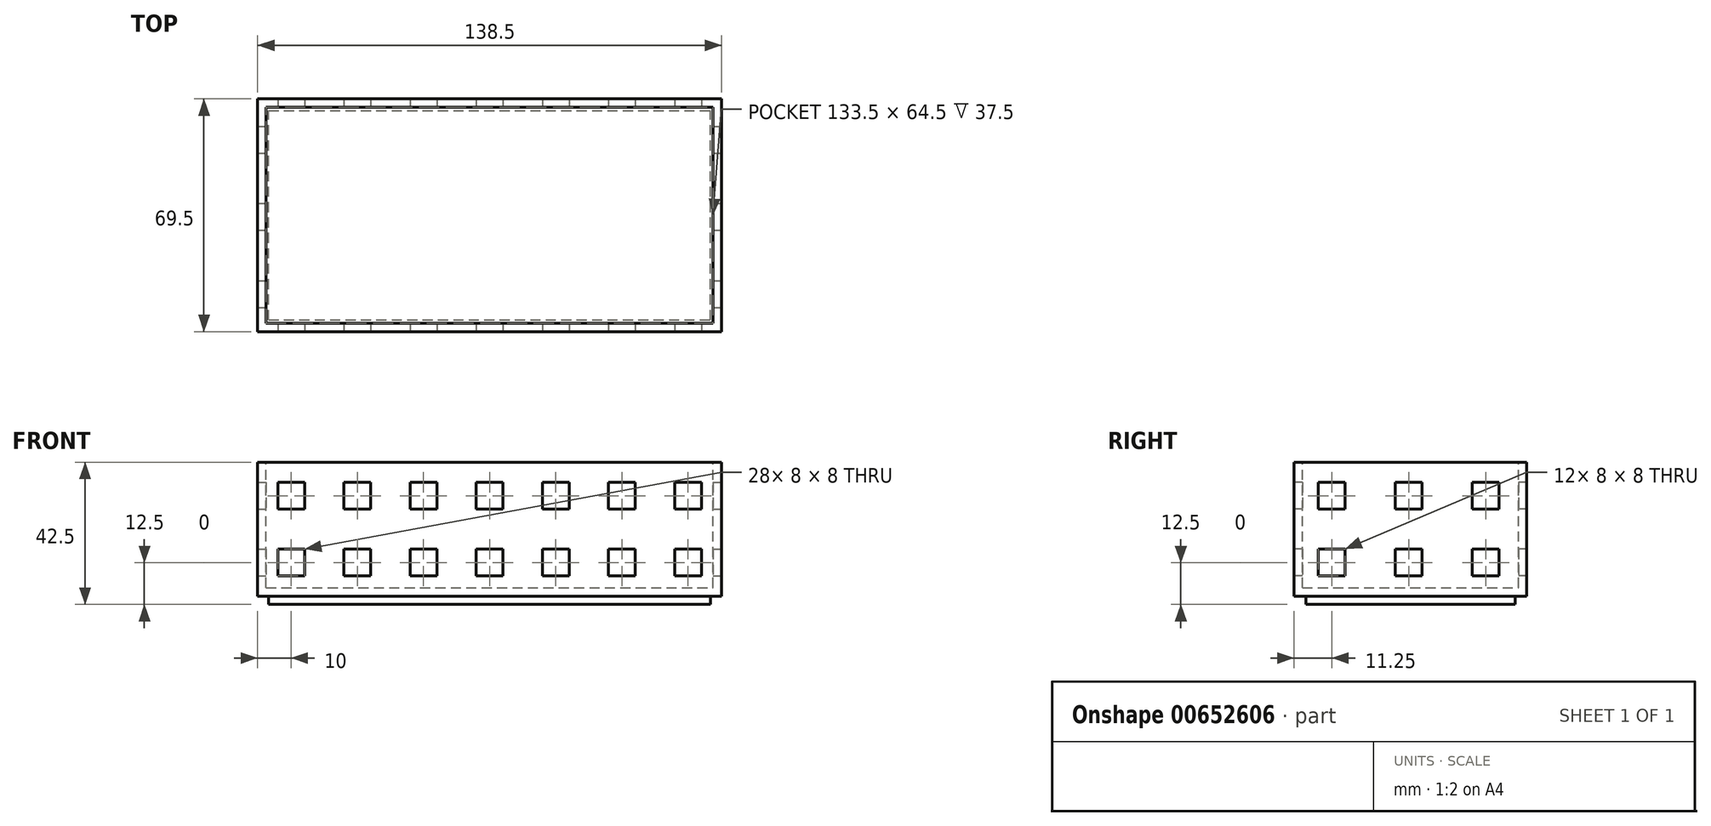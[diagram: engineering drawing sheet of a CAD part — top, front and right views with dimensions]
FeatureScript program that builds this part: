
annotation { "Feature Type Name" : "Feature", "Feature Type Description" : "" }
export const myFeature = defineFeature(function(context is Context, id is Id, definition is map)
    precondition{}
    {
        {
            var Q0;
            Q0=qCreatedBy(makeId("Top.planeOp"),FACE);
            var sketch = newSketch(context, id + "F0", { "sketchPlane" : qUnion([Q0])});
            skLineSegment(sketch, "E0.bottom", {"start": v(0, 0) * mm, "end": v(138.5, 0) * mm});
            skLineSegment(sketch, "E0.top", {"start": v(0, 69.5) * mm, "end": v(138.5, 69.5) * mm});
            skLineSegment(sketch, "E0.left", {"start": v(0, 0) * mm, "end": v(0, 69.5) * mm});
            skLineSegment(sketch, "E0.right", {"start": v(138.5, 0) * mm, "end": v(138.5, 69.5) * mm});
            skSolve(sketch);
        }
        {
            var Q0;
            Q0=makeQuery(id+"F0.imprint","IMPRINT",FACE,{"disambiguationData":[TD([[makeQuery(id+"F0.imprint","IMPRINT",EDGE,{"derivedFrom":sQuery(id+"F0.wireOp",EDGE,"E0.bottom")}),1.0]])]});
            extrude(context, id + "F1", {"entities" : qUnion([Q0]), "depth" : 40 * mm, "offsetDistance" : 25 * mm});
        }
        {
            var Q0;
            Q0=makeQuery(id+"F1.opExtrude","CAP_FACE",FACE,{"disambiguationData":[OSD([sQuery(id+"F0.wireOp",EDGE,"E0.bottom"),sQuery(id+"F0.wireOp",EDGE,"E0.top"),sQuery(id+"F0.wireOp",EDGE,"E0.left"),sQuery(id+"F0.wireOp",EDGE,"E0.right")])],"isStart":false});
            var sketch = newSketch(context, id + "F2", { "sketchPlane" : qUnion([Q0])});
            skLineSegment(sketch, "E1.bottom", {"start": v(2.5, 2.5) * mm, "end": v(136, 2.5) * mm});
            skLineSegment(sketch, "E1.top", {"start": v(2.5, 67) * mm, "end": v(136, 67) * mm});
            skLineSegment(sketch, "E1.left", {"start": v(2.5, 2.5) * mm, "end": v(2.5, 67) * mm});
            skLineSegment(sketch, "E1.right", {"start": v(136, 2.5) * mm, "end": v(136, 67) * mm});
            skSolve(sketch);
        }
        {
            var Q0;
            Q0=makeQuery(id+"F2.imprint","IMPRINT",FACE,{"disambiguationData":[TD([[makeQuery(id+"F2.imprint","IMPRINT",EDGE,{"derivedFrom":sQuery(id+"F2.wireOp",EDGE,"E1.bottom")}),1.0]])]});
            extrude(context, id + "F3", {"entities" : qUnion([Q0]), "operationType" : NewBodyOperationType.REMOVE, "oppositeDirection" : true, "depth" : 37.5 * mm, "offsetDistance" : 25 * mm});
        }
        {
            var Q0;
            Q0=makeQuery(id+"F1.opExtrude","CAP_FACE",FACE,{"disambiguationData":[OSD([sQuery(id+"F0.wireOp",EDGE,"E0.bottom"),sQuery(id+"F0.wireOp",EDGE,"E0.top"),sQuery(id+"F0.wireOp",EDGE,"E0.left"),sQuery(id+"F0.wireOp",EDGE,"E0.right")])],"isStart":true});
            var sketch = newSketch(context, id + "F4", { "sketchPlane" : qUnion([Q0])});
            skLineSegment(sketch, "E2.bottom", {"start": v(3.25, -3.5) * mm, "end": v(135.25, -3.5) * mm});
            skLineSegment(sketch, "E2.top", {"start": v(3.25, -66) * mm, "end": v(135.25, -66) * mm});
            skLineSegment(sketch, "E2.left", {"start": v(3.25, -3.5) * mm, "end": v(3.25, -66) * mm});
            skLineSegment(sketch, "E2.right", {"start": v(135.25, -3.5) * mm, "end": v(135.25, -66) * mm});
            skSolve(sketch);
        }
        {
            var Q0;
            Q0=makeQuery(id+"F4.imprint","IMPRINT",FACE,{"disambiguationData":[TD([[makeQuery(id+"F4.imprint","IMPRINT",EDGE,{"derivedFrom":sQuery(id+"F4.wireOp",EDGE,"E2.bottom")}),-1.0]])]});
            extrude(context, id + "F5", {"entities" : qUnion([Q0]), "operationType" : NewBodyOperationType.ADD, "depth" : 2.5 * mm, "offsetDistance" : 25 * mm});
        }
        {
            var Q0;
            Q0=makeQuery(id+"F1.opExtrude","SWEPT_FACE",FACE,{"disambiguationData":[OSD([sQuery(id+"F0.wireOp",EDGE,"E0.right")])]});
            var sketch = newSketch(context, id + "F6", { "sketchPlane" : qUnion([Q0])});
            skLineSegment(sketch, "E3.bottom", {"start": v(7.25, 34) * mm, "end": v(15.25, 34) * mm});
            skLineSegment(sketch, "E3.top", {"start": v(7.25, 26) * mm, "end": v(15.25, 26) * mm});
            skLineSegment(sketch, "E3.left", {"start": v(7.25, 34) * mm, "end": v(7.25, 26) * mm});
            skLineSegment(sketch, "E3.right", {"start": v(15.25, 34) * mm, "end": v(15.25, 26) * mm});
            skLineSegment(sketch, "E4.bottom", {"start": v(30.25, 34) * mm, "end": v(38.25, 34) * mm});
            skLineSegment(sketch, "E4.top", {"start": v(30.25, 26) * mm, "end": v(38.25, 26) * mm});
            skLineSegment(sketch, "E4.left", {"start": v(30.25, 34) * mm, "end": v(30.25, 26) * mm});
            skLineSegment(sketch, "E4.right", {"start": v(38.25, 34) * mm, "end": v(38.25, 26) * mm});
            skLineSegment(sketch, "E5.bottom", {"start": v(53.25, 34) * mm, "end": v(61.25, 34) * mm});
            skLineSegment(sketch, "E5.top", {"start": v(53.25, 26) * mm, "end": v(61.25, 26) * mm});
            skLineSegment(sketch, "E5.left", {"start": v(53.25, 34) * mm, "end": v(53.25, 26) * mm});
            skLineSegment(sketch, "E5.right", {"start": v(61.25, 34) * mm, "end": v(61.25, 26) * mm});
            skLineSegment(sketch, "E6.bottom", {"start": v(7.25, 14) * mm, "end": v(15.25, 14) * mm});
            skLineSegment(sketch, "E6.top", {"start": v(7.25, 6) * mm, "end": v(15.25, 6) * mm});
            skLineSegment(sketch, "E6.left", {"start": v(7.25, 14) * mm, "end": v(7.25, 6) * mm});
            skLineSegment(sketch, "E6.right", {"start": v(15.25, 14) * mm, "end": v(15.25, 6) * mm});
            skLineSegment(sketch, "E7.bottom", {"start": v(30.25, 14) * mm, "end": v(38.25, 14) * mm});
            skLineSegment(sketch, "E7.top", {"start": v(30.25, 6) * mm, "end": v(38.25, 6) * mm});
            skLineSegment(sketch, "E7.left", {"start": v(30.25, 14) * mm, "end": v(30.25, 6) * mm});
            skLineSegment(sketch, "E7.right", {"start": v(38.25, 14) * mm, "end": v(38.25, 6) * mm});
            skLineSegment(sketch, "E8.bottom", {"start": v(53.25, 14) * mm, "end": v(61.25, 14) * mm});
            skLineSegment(sketch, "E8.top", {"start": v(53.25, 6) * mm, "end": v(61.25, 6) * mm});
            skLineSegment(sketch, "E8.left", {"start": v(53.25, 14) * mm, "end": v(53.25, 6) * mm});
            skLineSegment(sketch, "E8.right", {"start": v(61.25, 14) * mm, "end": v(61.25, 6) * mm});
            skSolve(sketch);
        }
        {
            var Q0;
            Q0=makeQuery(id+"F6.imprint","IMPRINT",FACE,{"disambiguationData":[TD([[makeQuery(id+"F6.imprint","IMPRINT",EDGE,{"derivedFrom":sQuery(id+"F6.wireOp",EDGE,"E3.bottom")}),-1.0]])]});
            var Q1;
            Q1=makeQuery(id+"F6.imprint","IMPRINT",FACE,{"disambiguationData":[TD([[makeQuery(id+"F6.imprint","IMPRINT",EDGE,{"derivedFrom":sQuery(id+"F6.wireOp",EDGE,"E6.bottom")}),-1.0]])]});
            var Q2;
            Q2=makeQuery(id+"F6.imprint","IMPRINT",FACE,{"disambiguationData":[TD([[makeQuery(id+"F6.imprint","IMPRINT",EDGE,{"derivedFrom":sQuery(id+"F6.wireOp",EDGE,"E8.bottom")}),-1.0]])]});
            var Q3;
            Q3=makeQuery(id+"F6.imprint","IMPRINT",FACE,{"disambiguationData":[TD([[makeQuery(id+"F6.imprint","IMPRINT",EDGE,{"derivedFrom":sQuery(id+"F6.wireOp",EDGE,"E5.bottom")}),-1.0]])]});
            var Q4;
            Q4=makeQuery(id+"F6.imprint","IMPRINT",FACE,{"disambiguationData":[TD([[makeQuery(id+"F6.imprint","IMPRINT",EDGE,{"derivedFrom":sQuery(id+"F6.wireOp",EDGE,"E4.bottom")}),-1.0]])]});
            var Q5;
            Q5=makeQuery(id+"F6.imprint","IMPRINT",FACE,{"disambiguationData":[TD([[makeQuery(id+"F6.imprint","IMPRINT",EDGE,{"derivedFrom":sQuery(id+"F6.wireOp",EDGE,"E7.bottom")}),-1.0]])]});
            extrude(context, id + "F7", {"entities" : qUnion([Q0, Q1, Q2, Q3, Q4, Q5]), "operationType" : NewBodyOperationType.REMOVE, "oppositeDirection" : true, "depth" : 138.5 * mm, "offsetDistance" : 25 * mm});
        }
        {
            var Q0;
            Q0=makeQuery(id+"F1.opExtrude","SWEPT_FACE",FACE,{"disambiguationData":[OSD([sQuery(id+"F0.wireOp",EDGE,"E0.bottom")])]});
            var sketch = newSketch(context, id + "F8", { "sketchPlane" : qUnion([Q0])});
            skLineSegment(sketch, "E9.bottom", {"start": v(6, 34) * mm, "end": v(14, 34) * mm});
            skLineSegment(sketch, "E9.top", {"start": v(6, 26) * mm, "end": v(14, 26) * mm});
            skLineSegment(sketch, "E9.left", {"start": v(6, 34) * mm, "end": v(6, 26) * mm});
            skLineSegment(sketch, "E9.right", {"start": v(14, 34) * mm, "end": v(14, 26) * mm});
            skLineSegment(sketch, "E10.bottom", {"start": v(25.75, 34) * mm, "end": v(33.75, 34) * mm});
            skLineSegment(sketch, "E10.top", {"start": v(25.75, 26) * mm, "end": v(33.75, 26) * mm});
            skLineSegment(sketch, "E10.left", {"start": v(25.75, 34) * mm, "end": v(25.75, 26) * mm});
            skLineSegment(sketch, "E10.right", {"start": v(33.75, 34) * mm, "end": v(33.75, 26) * mm});
            skLineSegment(sketch, "E11.bottom", {"start": v(45.5, 34) * mm, "end": v(53.5, 34) * mm});
            skLineSegment(sketch, "E11.top", {"start": v(45.5, 26) * mm, "end": v(53.5, 26) * mm});
            skLineSegment(sketch, "E11.left", {"start": v(45.5, 34) * mm, "end": v(45.5, 26) * mm});
            skLineSegment(sketch, "E11.right", {"start": v(53.5, 34) * mm, "end": v(53.5, 26) * mm});
            skLineSegment(sketch, "E12.bottom", {"start": v(65.25, 34) * mm, "end": v(73.25, 34) * mm});
            skLineSegment(sketch, "E12.top", {"start": v(65.25, 26) * mm, "end": v(73.25, 26) * mm});
            skLineSegment(sketch, "E12.left", {"start": v(65.25, 34) * mm, "end": v(65.25, 26) * mm});
            skLineSegment(sketch, "E12.right", {"start": v(73.25, 34) * mm, "end": v(73.25, 26) * mm});
            skLineSegment(sketch, "E13.bottom", {"start": v(85, 34) * mm, "end": v(93, 34) * mm});
            skLineSegment(sketch, "E13.top", {"start": v(85, 26) * mm, "end": v(93, 26) * mm});
            skLineSegment(sketch, "E13.left", {"start": v(85, 34) * mm, "end": v(85, 26) * mm});
            skLineSegment(sketch, "E13.right", {"start": v(93, 34) * mm, "end": v(93, 26) * mm});
            skLineSegment(sketch, "E14.bottom", {"start": v(104.75, 34) * mm, "end": v(112.75, 34) * mm});
            skLineSegment(sketch, "E14.top", {"start": v(104.75, 26) * mm, "end": v(112.75, 26) * mm});
            skLineSegment(sketch, "E14.left", {"start": v(104.75, 34) * mm, "end": v(104.75, 26) * mm});
            skLineSegment(sketch, "E14.right", {"start": v(112.75, 34) * mm, "end": v(112.75, 26) * mm});
            skLineSegment(sketch, "E15.bottom", {"start": v(124.5, 34) * mm, "end": v(132.5, 34) * mm});
            skLineSegment(sketch, "E15.top", {"start": v(124.5, 26) * mm, "end": v(132.5, 26) * mm});
            skLineSegment(sketch, "E15.left", {"start": v(132.5, 34) * mm, "end": v(132.5, 26) * mm});
            skLineSegment(sketch, "E15.right", {"start": v(124.5, 34) * mm, "end": v(124.5, 26) * mm});
            skLineSegment(sketch, "E16.bottom", {"start": v(6, 14) * mm, "end": v(14, 14) * mm});
            skLineSegment(sketch, "E16.top", {"start": v(6, 6) * mm, "end": v(14, 6) * mm});
            skLineSegment(sketch, "E16.left", {"start": v(6, 14) * mm, "end": v(6, 6) * mm});
            skLineSegment(sketch, "E16.right", {"start": v(14, 14) * mm, "end": v(14, 6) * mm});
            skLineSegment(sketch, "E17.bottom", {"start": v(25.75, 14) * mm, "end": v(33.75, 14) * mm});
            skLineSegment(sketch, "E17.top", {"start": v(25.75, 6) * mm, "end": v(33.75, 6) * mm});
            skLineSegment(sketch, "E17.left", {"start": v(25.75, 14) * mm, "end": v(25.75, 6) * mm});
            skLineSegment(sketch, "E17.right", {"start": v(33.75, 14) * mm, "end": v(33.75, 6) * mm});
            skLineSegment(sketch, "E18.bottom", {"start": v(45.5, 14) * mm, "end": v(53.5, 14) * mm});
            skLineSegment(sketch, "E18.top", {"start": v(45.5, 6) * mm, "end": v(53.5, 6) * mm});
            skLineSegment(sketch, "E18.left", {"start": v(45.5, 14) * mm, "end": v(45.5, 6) * mm});
            skLineSegment(sketch, "E18.right", {"start": v(53.5, 14) * mm, "end": v(53.5, 6) * mm});
            skLineSegment(sketch, "E19.bottom", {"start": v(65.25, 14) * mm, "end": v(73.25, 14) * mm});
            skLineSegment(sketch, "E19.top", {"start": v(65.25, 6) * mm, "end": v(73.25, 6) * mm});
            skLineSegment(sketch, "E19.left", {"start": v(65.25, 14) * mm, "end": v(65.25, 6) * mm});
            skLineSegment(sketch, "E19.right", {"start": v(73.25, 14) * mm, "end": v(73.25, 6) * mm});
            skLineSegment(sketch, "E20.bottom", {"start": v(85, 14) * mm, "end": v(93, 14) * mm});
            skLineSegment(sketch, "E20.top", {"start": v(85, 6) * mm, "end": v(93, 6) * mm});
            skLineSegment(sketch, "E20.left", {"start": v(85, 14) * mm, "end": v(85, 6) * mm});
            skLineSegment(sketch, "E20.right", {"start": v(93, 14) * mm, "end": v(93, 6) * mm});
            skLineSegment(sketch, "E21.bottom", {"start": v(104.75, 14) * mm, "end": v(112.75, 14) * mm});
            skLineSegment(sketch, "E21.top", {"start": v(104.75, 6) * mm, "end": v(112.75, 6) * mm});
            skLineSegment(sketch, "E21.left", {"start": v(104.75, 14) * mm, "end": v(104.75, 6) * mm});
            skLineSegment(sketch, "E21.right", {"start": v(112.75, 14) * mm, "end": v(112.75, 6) * mm});
            skLineSegment(sketch, "E22.bottom", {"start": v(124.5, 14) * mm, "end": v(132.5, 14) * mm});
            skLineSegment(sketch, "E22.top", {"start": v(124.5, 6) * mm, "end": v(132.5, 6) * mm});
            skLineSegment(sketch, "E22.left", {"start": v(124.5, 14) * mm, "end": v(124.5, 6) * mm});
            skLineSegment(sketch, "E22.right", {"start": v(132.5, 14) * mm, "end": v(132.5, 6) * mm});
            skSolve(sketch);
        }
        {
            var Q0;
            Q0=makeQuery(id+"F8.imprint","IMPRINT",FACE,{"disambiguationData":[TD([[makeQuery(id+"F8.imprint","IMPRINT",EDGE,{"derivedFrom":sQuery(id+"F8.wireOp",EDGE,"E9.bottom")}),-1.0]])]});
            var Q1;
            Q1=makeQuery(id+"F8.imprint","IMPRINT",FACE,{"disambiguationData":[TD([[makeQuery(id+"F8.imprint","IMPRINT",EDGE,{"derivedFrom":sQuery(id+"F8.wireOp",EDGE,"E16.bottom")}),-1.0]])]});
            var Q2;
            Q2=makeQuery(id+"F8.imprint","IMPRINT",FACE,{"disambiguationData":[TD([[makeQuery(id+"F8.imprint","IMPRINT",EDGE,{"derivedFrom":sQuery(id+"F8.wireOp",EDGE,"E17.bottom")}),-1.0]])]});
            var Q3;
            Q3=makeQuery(id+"F8.imprint","IMPRINT",FACE,{"disambiguationData":[TD([[makeQuery(id+"F8.imprint","IMPRINT",EDGE,{"derivedFrom":sQuery(id+"F8.wireOp",EDGE,"E10.bottom")}),-1.0]])]});
            var Q4;
            Q4=makeQuery(id+"F8.imprint","IMPRINT",FACE,{"disambiguationData":[TD([[makeQuery(id+"F8.imprint","IMPRINT",EDGE,{"derivedFrom":sQuery(id+"F8.wireOp",EDGE,"E11.bottom")}),-1.0]])]});
            var Q5;
            Q5=makeQuery(id+"F8.imprint","IMPRINT",FACE,{"disambiguationData":[TD([[makeQuery(id+"F8.imprint","IMPRINT",EDGE,{"derivedFrom":sQuery(id+"F8.wireOp",EDGE,"E18.bottom")}),-1.0]])]});
            var Q6;
            Q6=makeQuery(id+"F8.imprint","IMPRINT",FACE,{"disambiguationData":[TD([[makeQuery(id+"F8.imprint","IMPRINT",EDGE,{"derivedFrom":sQuery(id+"F8.wireOp",EDGE,"E19.bottom")}),-1.0]])]});
            var Q7;
            Q7=makeQuery(id+"F8.imprint","IMPRINT",FACE,{"disambiguationData":[TD([[makeQuery(id+"F8.imprint","IMPRINT",EDGE,{"derivedFrom":sQuery(id+"F8.wireOp",EDGE,"E12.bottom")}),-1.0]])]});
            var Q8;
            Q8=makeQuery(id+"F8.imprint","IMPRINT",FACE,{"disambiguationData":[TD([[makeQuery(id+"F8.imprint","IMPRINT",EDGE,{"derivedFrom":sQuery(id+"F8.wireOp",EDGE,"E13.bottom")}),-1.0]])]});
            var Q9;
            Q9=makeQuery(id+"F8.imprint","IMPRINT",FACE,{"disambiguationData":[TD([[makeQuery(id+"F8.imprint","IMPRINT",EDGE,{"derivedFrom":sQuery(id+"F8.wireOp",EDGE,"E20.bottom")}),-1.0]])]});
            var Q10;
            Q10=makeQuery(id+"F8.imprint","IMPRINT",FACE,{"disambiguationData":[TD([[makeQuery(id+"F8.imprint","IMPRINT",EDGE,{"derivedFrom":sQuery(id+"F8.wireOp",EDGE,"E21.bottom")}),-1.0]])]});
            var Q11;
            Q11=makeQuery(id+"F8.imprint","IMPRINT",FACE,{"disambiguationData":[TD([[makeQuery(id+"F8.imprint","IMPRINT",EDGE,{"derivedFrom":sQuery(id+"F8.wireOp",EDGE,"E14.bottom")}),-1.0]])]});
            var Q12;
            Q12=makeQuery(id+"F8.imprint","IMPRINT",FACE,{"disambiguationData":[TD([[makeQuery(id+"F8.imprint","IMPRINT",EDGE,{"derivedFrom":sQuery(id+"F8.wireOp",EDGE,"E15.bottom")}),-1.0]])]});
            var Q13;
            Q13=makeQuery(id+"F8.imprint","IMPRINT",FACE,{"disambiguationData":[TD([[makeQuery(id+"F8.imprint","IMPRINT",EDGE,{"derivedFrom":sQuery(id+"F8.wireOp",EDGE,"E22.bottom")}),-1.0]])]});
            extrude(context, id + "F9", {"entities" : qUnion([Q0, Q1, Q2, Q3, Q4, Q5, Q6, Q7, Q8, Q9, Q10, Q11, Q12, Q13]), "operationType" : NewBodyOperationType.REMOVE, "oppositeDirection" : true, "depth" : 69.5 * mm, "offsetDistance" : 25 * mm});
        }
    });
